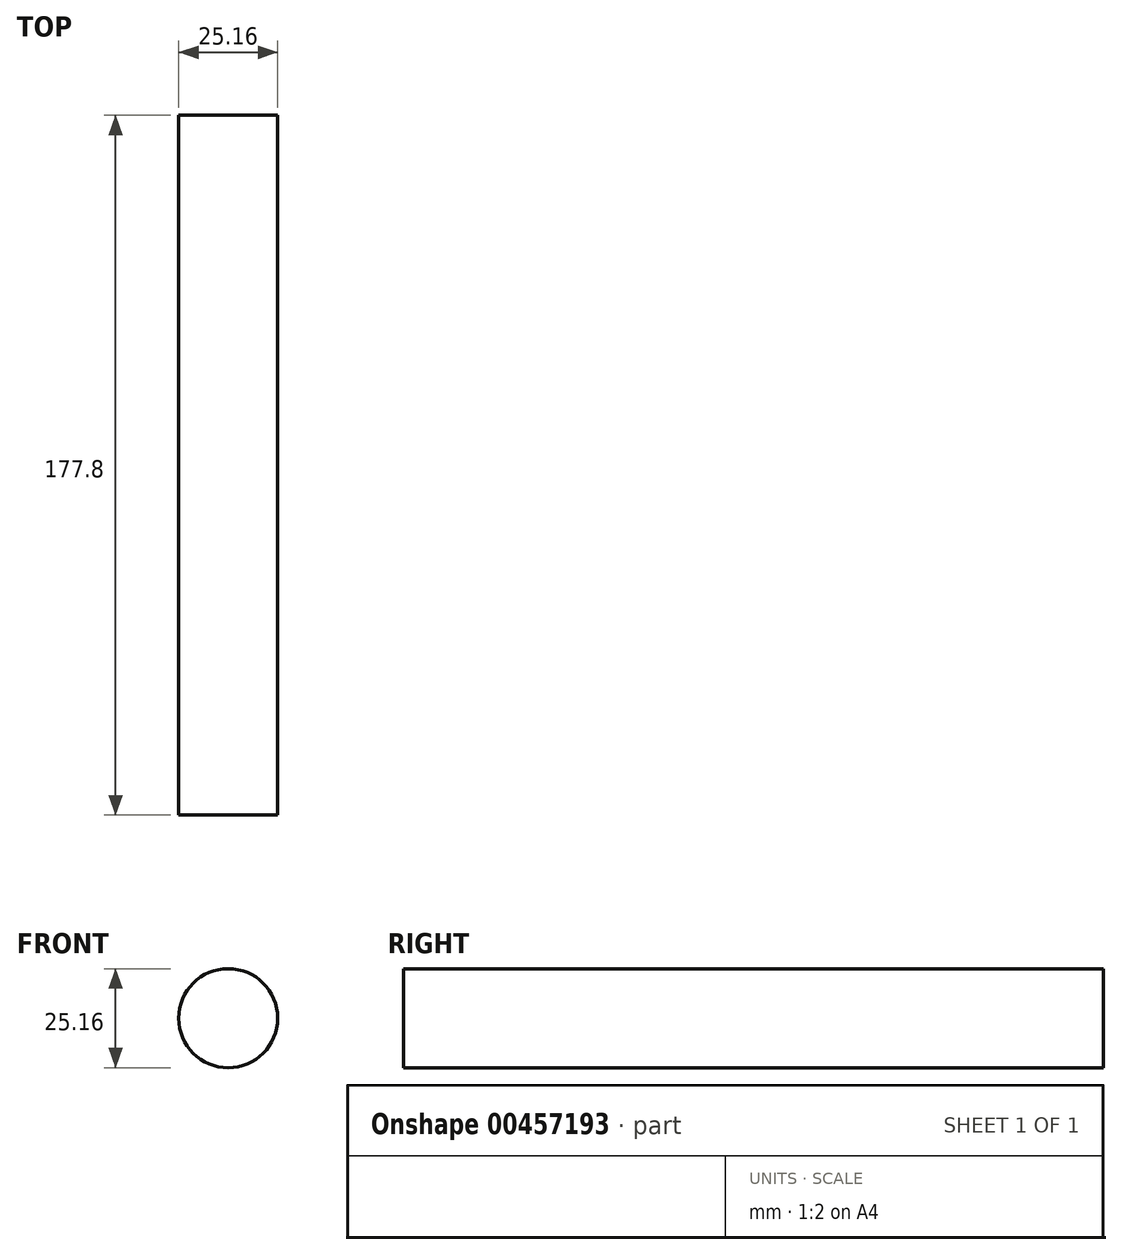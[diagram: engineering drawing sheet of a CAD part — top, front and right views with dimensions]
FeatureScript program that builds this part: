
annotation { "Feature Type Name" : "Feature", "Feature Type Description" : "" }
export const myFeature = defineFeature(function(context is Context, id is Id, definition is map)
    precondition{}
    {
        {
            var Q0;
            Q0=qCreatedBy(makeId("Front.planeOp"),FACE);
            var sketch = newSketch(context, id + "F0", { "sketchPlane" : qUnion([Q0])});
            skCircle(sketch, "E0", {"center": v(-26.76, 16) * mm, "radius": 12.58 * mm});
            skSolve(sketch);
        }
        {
            var Q0;
            Q0=makeQuery(id+"F0.imprint","IMPRINT",FACE,{"disambiguationData":[TD([[makeQuery(id+"F0.imprint","IMPRINT",EDGE,{"derivedFrom":sQuery(id+"F0.wireOp",EDGE,"E0")}),1.0]])]});
            extrude(context, id + "F1", {"entities" : qUnion([Q0]), "depth" : 177.8 * mm});
        }
    });
